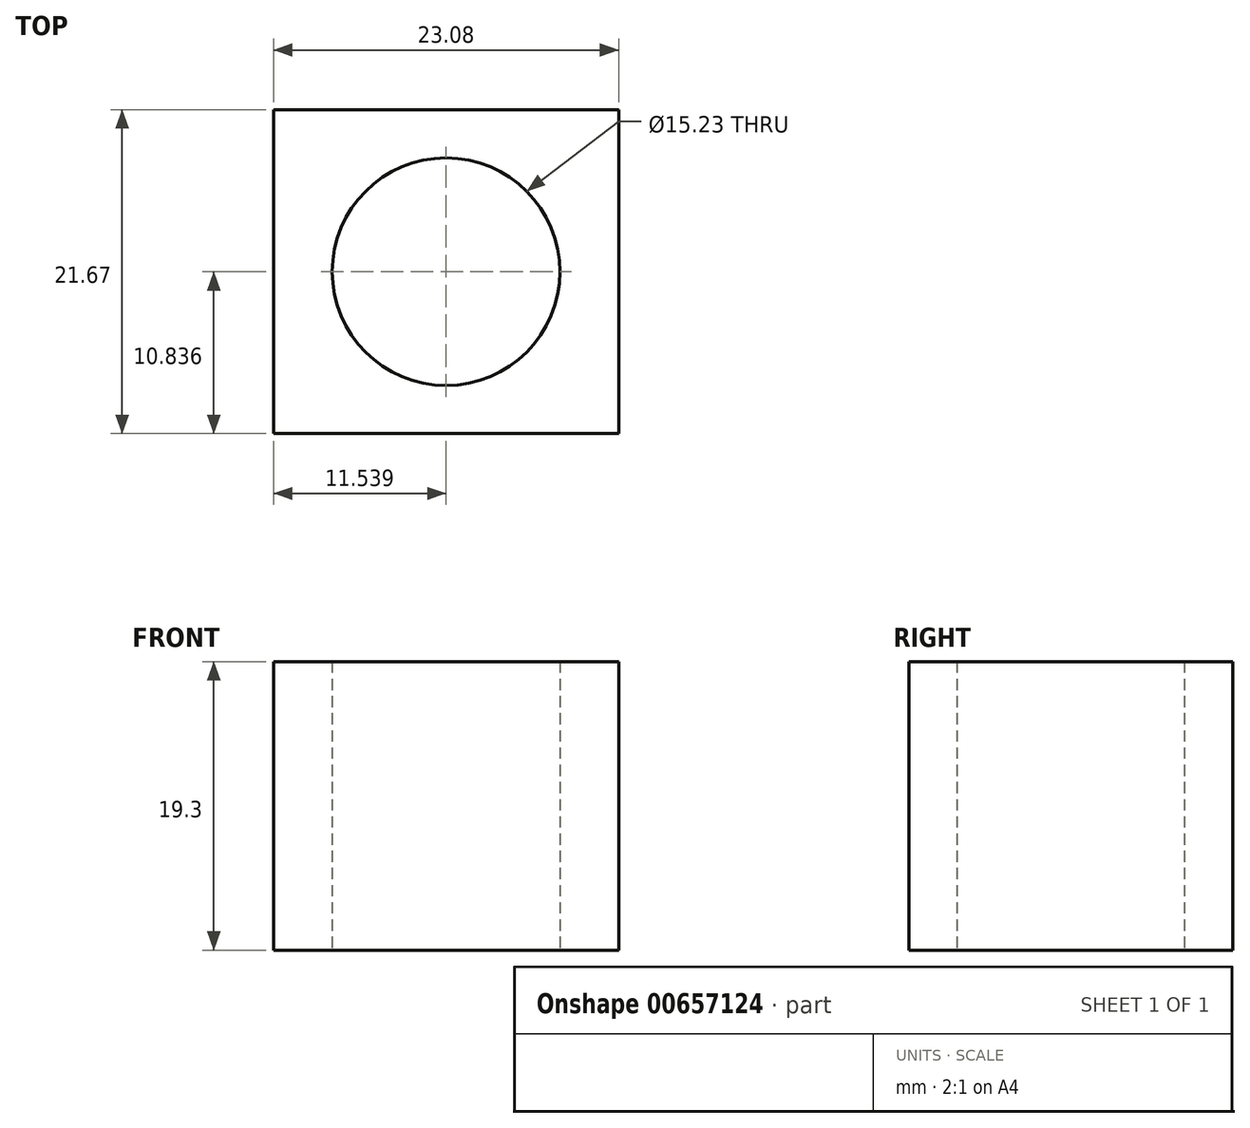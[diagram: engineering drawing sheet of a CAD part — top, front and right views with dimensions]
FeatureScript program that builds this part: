
annotation { "Feature Type Name" : "Feature", "Feature Type Description" : "" }
export const myFeature = defineFeature(function(context is Context, id is Id, definition is map)
    precondition{}
    {
        {
            var Q0;
            Q0=qCreatedBy(makeId("Top.planeOp"),FACE);
            var sketch = newSketch(context, id + "F0", { "sketchPlane" : qUnion([Q0])});
            skLineSegment(sketch, "E0.bottom", {"start": v(-48.2, 45.58) * mm, "end": v(-25.12, 45.58) * mm});
            skLineSegment(sketch, "E0.top", {"start": v(-48.2, 23.91) * mm, "end": v(-25.12, 23.91) * mm});
            skLineSegment(sketch, "E0.left", {"start": v(-48.2, 45.58) * mm, "end": v(-48.2, 23.91) * mm});
            skLineSegment(sketch, "E0.right", {"start": v(-25.12, 45.58) * mm, "end": v(-25.12, 23.91) * mm});
            skPoint(sketch, "E0.middle", {"position": v(-36.66, 34.75) * mm});
            skCircle(sketch, "E1", {"center": v(-36.66, 34.75) * mm, "radius": 7.61 * mm});
            skSolve(sketch);
        }
        {
            var Q0;
            Q0=makeQuery(id+"F0.imprint","IMPRINT",FACE,{"disambiguationData":[TD([[makeQuery(id+"F0.imprint","IMPRINT",EDGE,{"derivedFrom":sQuery(id+"F0.wireOp",EDGE,"E0.bottom")}),-1.0]])]});
            extrude(context, id + "F1", {"entities" : qUnion([Q0]), "depth" : 19.3 * mm, "offsetDistance" : 25 * mm});
        }
    });
